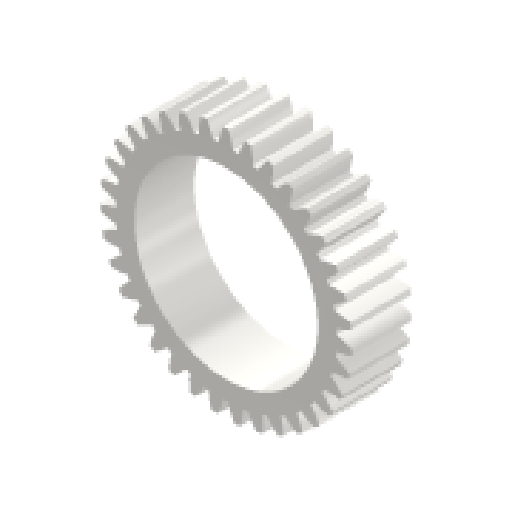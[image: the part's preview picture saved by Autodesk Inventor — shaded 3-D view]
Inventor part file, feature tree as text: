
AUTODESK INVENTOR PART (.ipt)
format: ipt  version: 2024.1 (Build 281209000, 209)  size: 288,768 bytes
history: native  units: mm (DEFAULTED — no unit token found)
features: plane x3, other x3, extrude x2, sketch x2, chamfer x1
ambient origin geometry x8: Origin, YZ Plane, XZ Plane, XY Plane, X Axis, Y Axis, Z Axis, Center Point
bodies: Solid1 (feature_tree)
feature tree (11):
  extrude  "Extrusion1"  Depth=10.0mm TaperAngle=0.0deg
  plane  "Work Plane2"
  plane  "Work Plane8"
  plane  "Work Plane9"
  other  "Stirnzahnrad"
  extrude  "Extrusion2"  Depth=10.0mm TaperAngle=0.0deg
  chamfer  "Fasen1"  Distance=35.0mm
  sketch  "Sketch1"  dims[d0=41.875mm d1=10.0mm d2=0.0mm]
  other  "Srf1"
  sketch  "Skizze3"  dims[d3=39.375mm d4=10.0mm d5=0.0mm d16=35.0mm d17=0.0mm d34=0.897598mm d39=0.0mm d41=0.0mm d43=35.0mm d46=35.0mm d47=0.0mm d48=0.0mm d49=30.5mm d50=10.0mm d51=0.0mm d52=1.0mm d53=2.0mm d54=45.0deg]
  other  "Flankendurchmesser"
